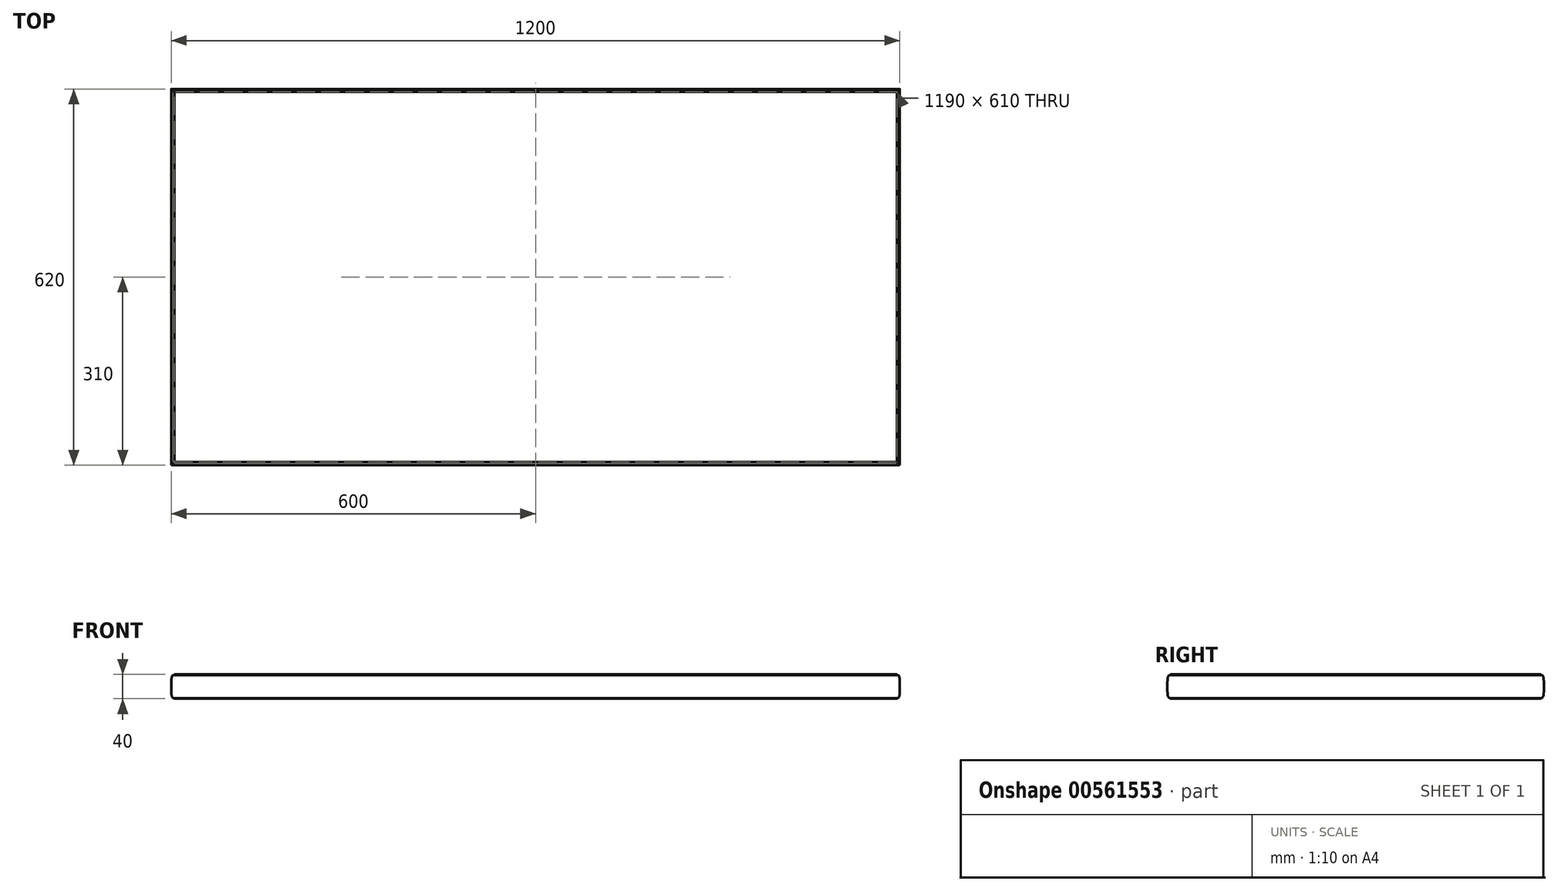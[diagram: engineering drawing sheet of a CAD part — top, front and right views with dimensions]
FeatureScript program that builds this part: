
annotation { "Feature Type Name" : "Feature", "Feature Type Description" : "" }
export const myFeature = defineFeature(function(context is Context, id is Id, definition is map)
    precondition{}
    {
        {
            var Q0;
            Q0=qCreatedBy(makeId("Top.planeOp"),FACE);
            var sketch = newSketch(context, id + "F0", { "sketchPlane" : qUnion([Q0])});
            skLineSegment(sketch, "E0.bottom", {"start": v(0, 0) * mm, "end": v(1200, 0) * mm});
            skLineSegment(sketch, "E0.top", {"start": v(0, 620) * mm, "end": v(1200, 620) * mm});
            skLineSegment(sketch, "E0.left", {"start": v(0, 0) * mm, "end": v(0, 620) * mm});
            skLineSegment(sketch, "E0.right", {"start": v(1200, 0) * mm, "end": v(1200, 620) * mm});
            skSolve(sketch);
        }
        {
            var Q0;
            Q0=makeQuery(id+"F0.imprint","IMPRINT",FACE,{"disambiguationData":[TD([[makeQuery(id+"F0.imprint","IMPRINT",EDGE,{"derivedFrom":sQuery(id+"F0.wireOp",EDGE,"E0.bottom")}),1.0]])]});
            extrude(context, id + "F1", {"entities" : qUnion([Q0]), "depth" : 40 * mm, "offsetDistance" : 25 * mm});
        }
        {
            var Q0;
            Q0=makeQuery(id+"F1.opExtrude","SWEPT_FACE",FACE,{"disambiguationData":[OSD([sQuery(id+"F0.wireOp",EDGE,"E0.bottom")])]});
            var sketch = newSketch(context, id + "F2", { "sketchPlane" : qUnion([Q0])});
            skLineSegment(sketch, "E1.top", {"start": v(4, 39) * mm, "end": v(5, 39) * mm});
            skLineSegment(sketch, "E1.right", {"start": v(5, 40) * mm, "end": v(5, 39) * mm});
            skLineSegment(sketch, "E2", {"start": v(-4.4, 20) * mm, "end": v(-21.1, 20) * mm, "construction": true});
            skPoint(sketch, "E2.startSnap0", {"position": v(0, 20) * mm});
            skLineSegment(sketch, "E3", {"start": v(0, 20) * mm, "end": v(0, 40) * mm});
            skLineSegment(sketch, "E4", {"start": v(0, 40) * mm, "end": v(5, 40) * mm});
            skFitSpline(sketch, "E5", {"points": [v(4, 39) * mm, v(0, 20) * mm], "startDerivative": vector(-12, 0) * mm, "endDerivative": vector(0, -34.33) * mm});
            skLineSegment(sketch, "E6", {"start": v(600, 69.25) * mm, "end": v(600, 184.03) * mm, "construction": true});
            skPoint(sketch, "E6.startSnap0", {"position": v(600, 40) * mm});
            skFitSpline(sketch, "E7.MirrorCS", {"points": [v(4, 1) * mm, v(0, 20) * mm], "startDerivative": vector(-12, 0) * mm, "endDerivative": vector(0, 34.33) * mm});
            skLineSegment(sketch, "E8.MirrorCS", {"start": v(4, 1) * mm, "end": v(5, 1) * mm});
            skLineSegment(sketch, "E9.MirrorCS", {"start": v(5, 0) * mm, "end": v(5, 1) * mm});
            skLineSegment(sketch, "E10.MirrorCS", {"start": v(0, 0) * mm, "end": v(5, 0) * mm});
            skLineSegment(sketch, "E11.MirrorCS", {"start": v(0, 20) * mm, "end": v(0, 0) * mm});
            skLineSegment(sketch, "E12.MirrorCS", {"start": v(1195, 0) * mm, "end": v(1195, 1) * mm});
            skLineSegment(sketch, "E13.MirrorCS", {"start": v(1196, 1) * mm, "end": v(1195, 1) * mm});
            skFitSpline(sketch, "E14.MirrorCS", {"points": [v(1196, 1) * mm, v(1200, 20) * mm], "startDerivative": vector(12, 0) * mm, "endDerivative": vector(0, 34.33) * mm});
            skLineSegment(sketch, "E15.MirrorCS", {"start": v(1200, 0) * mm, "end": v(1195, 0) * mm});
            skLineSegment(sketch, "E16.MirrorCS", {"start": v(1200, 20) * mm, "end": v(1200, 0) * mm});
            skFitSpline(sketch, "E17.MirrorCS", {"points": [v(1196, 39) * mm, v(1200, 20) * mm], "startDerivative": vector(12, 0) * mm, "endDerivative": vector(0, -34.33) * mm});
            skLineSegment(sketch, "E18.MirrorCS", {"start": v(1200, 20) * mm, "end": v(1200, 40) * mm});
            skLineSegment(sketch, "E19.MirrorCS", {"start": v(1200, 40) * mm, "end": v(1195, 40) * mm});
            skLineSegment(sketch, "E20.MirrorCS", {"start": v(1195, 40) * mm, "end": v(1195, 39) * mm});
            skLineSegment(sketch, "E21.MirrorCS", {"start": v(1196, 39) * mm, "end": v(1195, 39) * mm});
            skSolve(sketch);
        }
        {
            var Q0;
            Q0 = qSketchRegion(id + "F2", true);
            extrude(context, id + "F3", {"entities" : qUnion([Q0]), "operationType" : NewBodyOperationType.REMOVE, "endBound" : BoundingType.THROUGH_ALL, "oppositeDirection" : true, "depth" : 25 * mm, "offsetDistance" : 25 * mm});
        }
        {
            var Q0;
            Q0=makeQuery(id+"F3.boolean.opBoolean","COPY",FACE,{"derivedFrom":makeQuery(id+"F3.opExtrude","SWEPT_FACE",FACE,{"disambiguationData":[OSD([sQuery(id+"F2.wireOp",EDGE,"E1.right")])]})});
            cPlane(context, id + "F4", {"entities" : qUnion([Q0]), "cplaneType" : CPlaneType.OFFSET, "offset" : 5 * mm, "width" : 150 * mm, "height" : 150 * mm});
        }
        {
            var Q0;
            Q0=qCreatedBy(id+"F4.planeOp",FACE);
            var sketch = newSketch(context, id + "F5", { "sketchPlane" : qUnion([Q0])});
            skLineSegment(sketch, "E22.top", {"start": v(-616, 39) * mm, "end": v(-615, 39) * mm});
            skLineSegment(sketch, "E22.right", {"start": v(-615, 40) * mm, "end": v(-615, 39) * mm});
            skLineSegment(sketch, "E23", {"start": v(-620, 20) * mm, "end": v(-620, 40) * mm});
            skLineSegment(sketch, "E24", {"start": v(-620, 40) * mm, "end": v(-615, 40) * mm});
            skFitSpline(sketch, "E25", {"points": [v(-616, 39) * mm, v(-620, 20) * mm], "startDerivative": vector(-12, 0) * mm, "endDerivative": vector(0, -34.33) * mm});
            skLineSegment(sketch, "E26", {"start": v(-628.1, 20) * mm, "end": v(-641.46, 20) * mm, "construction": true});
            skFitSpline(sketch, "E27.MirrorCS", {"points": [v(-616, 1) * mm, v(-620, 20) * mm], "startDerivative": vector(-12, 0) * mm, "endDerivative": vector(0, 34.33) * mm});
            skLineSegment(sketch, "E28.MirrorCS", {"start": v(-620, 20) * mm, "end": v(-620, 0) * mm});
            skLineSegment(sketch, "E29.MirrorCS", {"start": v(-616, 1) * mm, "end": v(-615, 1) * mm});
            skLineSegment(sketch, "E30.MirrorCS", {"start": v(-615, 0) * mm, "end": v(-615, 1) * mm});
            skLineSegment(sketch, "E31.MirrorCS", {"start": v(-620, 0) * mm, "end": v(-615, 0) * mm});
            skLineSegment(sketch, "E32", {"start": v(-310, 70.7) * mm, "end": v(-310, 112.8) * mm, "construction": true});
            skLineSegment(sketch, "E33.MirrorCS", {"start": v(-5, 0) * mm, "end": v(-5, 1) * mm});
            skLineSegment(sketch, "E34.MirrorCS", {"start": v(-4, 1) * mm, "end": v(-5, 1) * mm});
            skLineSegment(sketch, "E35.MirrorCS", {"start": v(0, 0) * mm, "end": v(-5, 0) * mm});
            skFitSpline(sketch, "E36.MirrorCS", {"points": [v(-4, 1) * mm, v(0, 20) * mm], "startDerivative": vector(12, 0) * mm, "endDerivative": vector(0, 34.33) * mm});
            skLineSegment(sketch, "E37.MirrorCS", {"start": v(0, 20) * mm, "end": v(0, 0) * mm});
            skFitSpline(sketch, "E38.MirrorCS", {"points": [v(-4, 39) * mm, v(0, 20) * mm], "startDerivative": vector(12, 0) * mm, "endDerivative": vector(0, -34.33) * mm});
            skLineSegment(sketch, "E39.MirrorCS", {"start": v(-4, 39) * mm, "end": v(-5, 39) * mm});
            skLineSegment(sketch, "E40.MirrorCS", {"start": v(-5, 40) * mm, "end": v(-5, 39) * mm});
            skLineSegment(sketch, "E41.MirrorCS", {"start": v(0, 40) * mm, "end": v(-5, 40) * mm});
            skLineSegment(sketch, "E42.MirrorCS", {"start": v(0, 20) * mm, "end": v(0, 40) * mm});
            skSolve(sketch);
        }
        {
            var Q0;
            Q0 = qSketchRegion(id + "F5", true);
            extrude(context, id + "F6", {"entities" : qUnion([Q0]), "operationType" : NewBodyOperationType.REMOVE, "endBound" : BoundingType.THROUGH_ALL, "oppositeDirection" : true, "depth" : 25 * mm, "offsetDistance" : 25 * mm});
        }
    });
